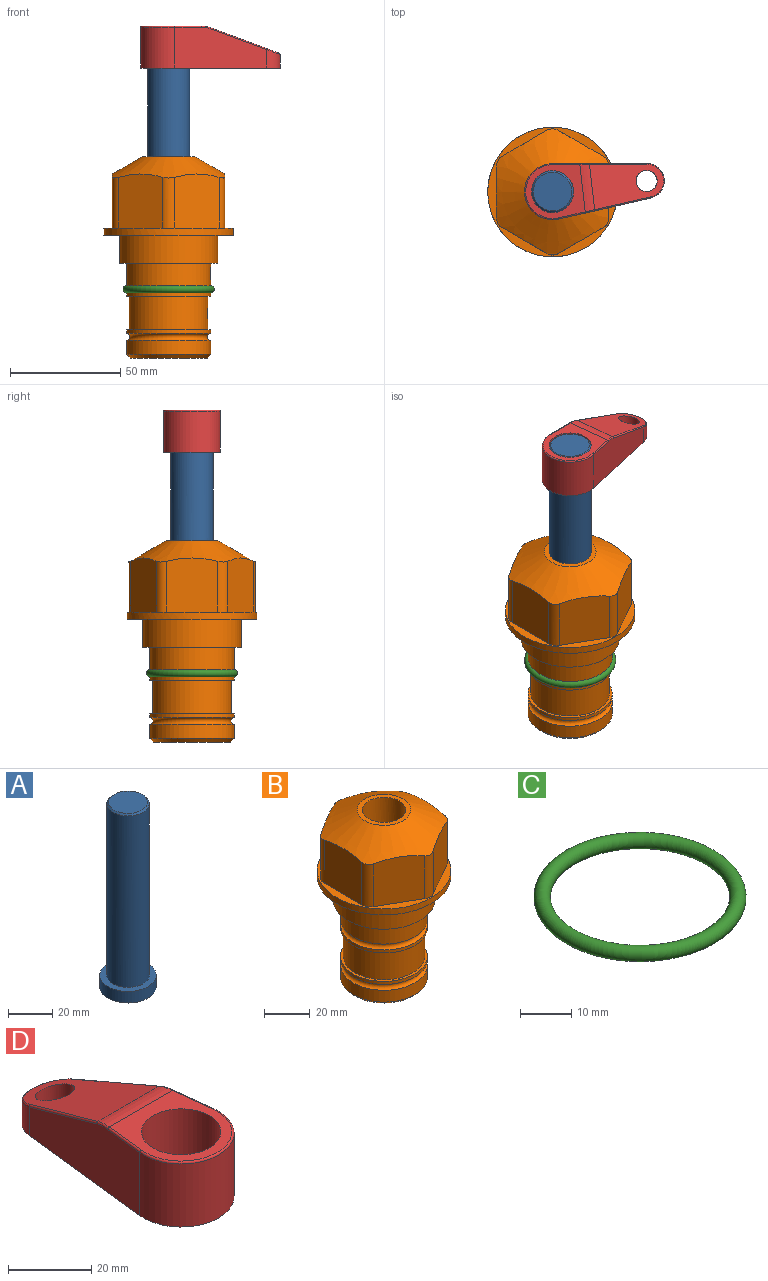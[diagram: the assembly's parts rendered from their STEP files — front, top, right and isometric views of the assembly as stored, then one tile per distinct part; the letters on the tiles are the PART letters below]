
ASSEMBLY  parts=4 mates=2
PART A: 6 faces, bbox 25.4x25.4x101.6 mm
  f0: plane 17.46x17.46mm, normal (0,0,1), area 239.5mm2, adj f5
  f1: plane 25.4x25.4mm, normal (0,0,-1), area 506.7mm2, adj f2
  f2: cylinder r=12.7mm len=25.4mm, axis (0,0,1), area 506.7mm2, adj f1,f3
  f3: plane 25.4x25.4mm, normal (0,0,1), area 221.7mm2, adj f2,f4
  f4: cylinder r=9.53mm len=94.46mm, axis (0,0,1), area 5653mm2, adj f3,f5
  f5: cone r=8.73mm half-angle=45deg, axis (0,0,-1), area 64.4mm2, adj f0,f4
PART B: 36 faces, bbox 58.7x58.7x91.2 mm
  f0: cylinder r=17.78mm len=35.56mm, axis (0,0,1), area 1670.8mm2, adj f23,f24,f31
  f1: cylinder r=19.05mm len=38.1mm, axis (0,0,1), area 1191.9mm2, adj f26,f27,f30
  f2: plane 58.66x58.66mm, normal (0,0,-1), area 1150.6mm2, adj f3,f28
  f3: cylinder r=29.33mm len=58.66mm, axis (0,0,-1), area 585.1mm2, adj f2,f4
  f4: plane 58.66x58.66mm, normal (0,0,1), area 475.9mm2, adj f3,f5,f6,f7,f8,f9,f10,f11
  f5: plane 24.5x20.32mm, normal (-0.5,0.87,0), area 562.8mm2, adj f4,f15,f16,f17
  f6: plane 24.5x20.32mm, normal (0.5,0.87,0), area 562.8mm2, adj f4,f14,f15,f17
  f7: plane 24.5x23.48mm, normal (1,0,0), area 562.8mm2, adj f4,f13,f14,f17
  f8: plane 24.5x20.32mm, normal (0.5,-0.87,0), area 562.8mm2, adj f4,f12,f13,f17
  f9: plane 24.5x20.32mm, normal (-0.5,-0.87,0), area 562.8mm2, adj f4,f11,f12,f17
  f10: plane 24.5x23.48mm, normal (-1,0,0), area 562.8mm2, adj f4,f11,f16,f17
  f11: cylinder r=5.08mm len=23.01mm, axis (0,0,-1), area 121.2mm2, adj f4,f9,f10,f17
  f12: cylinder r=5.08mm len=23.01mm, axis (0,0,-1), area 121.2mm2, adj f4,f8,f9,f17
  f13: cylinder r=5.08mm len=23.01mm, axis (0,0,-1), area 121.2mm2, adj f4,f7,f8,f17
  f14: cylinder r=5.08mm len=23.01mm, axis (0,0,-1), area 121.2mm2, adj f4,f6,f7,f17
  f15: cylinder r=5.08mm len=23.01mm, axis (0,0,-1), area 121.2mm2, adj f4,f5,f6,f17
  f16: cylinder r=5.08mm len=23.01mm, axis (0,0,-1), area 121.2mm2, adj f4,f5,f10,f17
  f17: cone r=11.73mm half-angle=60deg, axis (0,0,-1), area 2071.8mm2, adj f5,f6,f7,f8,f9,f10,f11,f12
  f18: plane 23.46x23.46mm, normal (0,0,1), area 147.4mm2, adj f17,f35
  f19: plane 34.93x34.93mm, normal (0,0,-1), area 958mm2, adj f29
  f20: cylinder r=19.05mm len=38.1mm, axis (0,0,1), area 760.1mm2, adj f21,f29
  f21: torus R=19.05mm, axis (0,0,1), area 565.3mm2, adj f20,f22
  f22: cylinder r=19.05mm len=38.1mm, axis (0,0,1), area 190mm2, adj f21,f23
  f23: plane 38.1x38.1mm, normal (0,0,1), area 146.9mm2, adj f0,f22
  f24: plane 38.1x38.1mm, normal (0,0,-1), area 146.9mm2, adj f0,f25
  f25: cylinder r=19.05mm len=38.1mm, axis (0,0,1), area 190mm2, adj f24,f26
  f26: torus R=19.05mm, axis (0,0,1), area 565.3mm2, adj f1,f25
  f27: plane 44.45x44.45mm, normal (0,0,-1), area 411.7mm2, adj f1,f28
  f28: cylinder r=22.23mm len=44.45mm, axis (0,0,1), area 1773.5mm2, adj f2,f27
  f29: cone r=19.05mm half-angle=45deg, axis (0,0,1), area 257.5mm2, adj f19,f20
  f30: cylinder r=3.17mm len=6.75mm, axis (-1,0,0), area 128mm2, adj f1,f33
  f31: cylinder r=3.17mm len=6.35mm, axis (-1,0,0), area 102.5mm2, adj f0,f33
  f32: plane 25.4x25.4mm, normal (0,0,1), area 506.7mm2, adj f33
  f33: cylinder r=12.7mm len=66.42mm, axis (0,0,-1), area 5236.2mm2, adj f30,f31,f32,f34
  f34: cone r=9.53mm half-angle=30deg, axis (0,0,-1), area 443.4mm2, adj f33,f35
  f35: cylinder r=9.53mm len=19.05mm, axis (0,0,-1), area 849mm2, adj f18,f34
PART C: 1 faces, bbox 44.7x44.7x3.2 mm
  f0: torus R=19.05mm, axis (0,0,1), area 1193.9mm2
PART D: 44 faces, bbox 27.5x64.5x19.1 mm
  f0: plane 2.3x0.95mm, normal (0,0,-1), area 1mm2, adj f25,f30,f34
  f1: plane 63.5x25.4mm, normal (0,0,-1), area 561.7mm2, adj f2,f3,f4,f5,f6,f7,f19,f20
  f2: cylinder r=12.7mm len=25.4mm, axis (0,0,-1), area 792.2mm2, adj f1,f3,f5,f13
  f3: plane 42.33x18.54mm, normal (0.99,0.11,0), area 647mm2, adj f1,f2,f4,f11,f12,f14
  f4: cylinder r=7.94mm len=15.78mm, axis (0,0,-1), area 158.6mm2, adj f1,f3,f5,f16
  f5: plane 42.33x18.54mm, normal (-0.99,0.11,0), area 647mm2, adj f1,f2,f4,f15,f17,f18
  f6: cylinder r=9.53mm len=19.05mm, axis (0,0,-1), area 1140.1mm2, adj f1,f8
  f7: cylinder r=4.76mm len=10.98mm, axis (0,0,-1), area 276.1mm2, adj f1,f9
  f8: plane 25.83x24.38mm, normal (0,0,1), area 262.2mm2, adj f6,f10,f11,f13,f15
  f9: plane 32.49x20.55mm, normal (0,0.34,0.94), area 489.9mm2, adj f7,f10,f14,f16,f18
  f10: cylinder r=12.7mm len=21.49mm, axis (-1,0,0), area 93.2mm2, adj f8,f9,f12,f17
  f11: cylinder r=0.51mm len=12.34mm, axis (0.11,-0.99,0), area 9.9mm2, adj f3,f8,f12,f13
  f12: bspline ~7.62x1.64mm, area 3.5mm2, adj f3,f10,f11,f14
  f13: torus R=12.19mm, axis (0,0,1), area 33.6mm2, adj f2,f8,f11,f15
  f14: cylinder r=0.51mm len=26.01mm, axis (0.1,-0.93,0.34), area 21.6mm2, adj f3,f9,f12,f16
  f15: cylinder r=0.51mm len=12.34mm, axis (0.11,0.99,0), area 9.9mm2, adj f5,f8,f13,f17
  f16: bspline ~15.78x7.05mm, area 15.7mm2, adj f4,f9,f14,f18
  f17: bspline ~7.62x1.64mm, area 3.5mm2, adj f5,f10,f15,f18
  f18: cylinder r=0.51mm len=26.01mm, axis (0.1,0.93,-0.34), area 21.6mm2, adj f5,f9,f16,f17
  f19: plane 21.6x14.29mm, normal (-0.99,-0.11,0), area 242.6mm2, adj f1,f26,f28,f34,f36,f38
  f20: plane 21.6x14.29mm, normal (0.99,-0.11,0), area 242.6mm2, adj f1,f27,f29,f37,f39,f41
  f21: cylinder r=12.7mm len=14.29mm, axis (0,0,-1), area 173.2mm2, adj f1,f26,f27,f30,f31,f33
  f22: cylinder r=7.94mm len=7.63mm, axis (0,0,-1), area 53.8mm2, adj f1,f28,f29,f42
  f23: plane 2.3x0.95mm, normal (0,0,-1), area 1mm2, adj f25,f33,f37
  f24: plane 17.94x12.32mm, normal (0,-0.34,-0.94), area 191.2mm2, adj f25,f38,f41,f42
  f25: cylinder r=9.53mm len=12.93mm, axis (-1,0,0), area 37.5mm2, adj f0,f23,f24,f31,f36,f39
  f26: cylinder r=1.59mm len=14.29mm, axis (0,0,-1), area 49mm2, adj f1,f19,f21,f32
  f27: cylinder r=1.59mm len=14.29mm, axis (0,0,-1), area 49mm2, adj f1,f20,f21,f35
  f28: cylinder r=1.59mm len=7.28mm, axis (0,0,-1), area 22.1mm2, adj f1,f19,f22,f40
  f29: cylinder r=1.59mm len=7.28mm, axis (0,0,-1), area 22.1mm2, adj f1,f20,f22,f43
  f30: torus R=14.29mm, axis (0,0,1), area 5.8mm2, adj f0,f21,f31,f32
  f31: bspline ~11.06x2.73mm, area 20.8mm2, adj f21,f25,f30,f33
  f32: sphere r=1.59mm, area 5.4mm2, adj f26,f30,f34
  f33: torus R=14.29mm, axis (0,0,1), area 5.8mm2, adj f21,f23,f31,f35
  f34: cylinder r=1.59mm len=1.68mm, axis (-0.11,0.99,0), area 2.4mm2, adj f0,f19,f32,f36
  f35: sphere r=1.59mm, area 5.4mm2, adj f27,f33,f37
  f36: bspline ~5.82x2.33mm, area 7.7mm2, adj f19,f25,f34,f38
  f37: cylinder r=1.59mm len=1.68mm, axis (0.11,0.99,0), area 2.4mm2, adj f20,f23,f35,f39
  f38: cylinder r=1.59mm len=18.33mm, axis (0.1,-0.93,0.34), area 46.7mm2, adj f19,f24,f36,f40
  f39: bspline ~5.82x2.33mm, area 7.7mm2, adj f20,f25,f37,f41
  f40: sphere r=1.59mm, area 3.6mm2, adj f28,f38,f42
  f41: cylinder r=1.59mm len=18.33mm, axis (0.1,0.93,-0.34), area 46.7mm2, adj f20,f24,f39,f43
  f42: bspline ~8.31x1.84mm, area 15.3mm2, adj f22,f24,f40,f43
  f43: sphere r=1.59mm, area 3.6mm2, adj f29,f41,f42
PLACE A rot(axis=(0,0,-1),83.5deg) t=(0,0,21)mm
PLACE B at identity fixed
PLACE C at identity
PLACE D rot(axis=(0,0,-1),83.5deg) t=(0,0,75.61)mm
MATE cylindrical A.f2 <-> B.f0  axis (0,0,1) through (0,0,46.64)mm
MATE fastened A.f2 <-> D.f2  axis (0,0,1) through (0,0,94.66)mm
